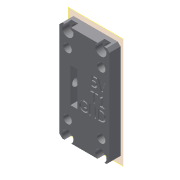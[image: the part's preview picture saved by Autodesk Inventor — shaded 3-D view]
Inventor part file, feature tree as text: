
AUTODESK INVENTOR PART (.ipt)
format: ipt  version: 2019 (Build 230136000, 136)  size: 431,104 bytes
history: native  units: mm
features: sketch x7, extrude x6, projected_geometry x5, other x3, plane x1, hole x1, reference x1
ambient origin geometry x8: Origin, YZ Plane, XZ Plane, XY Plane, X Axis, Y Axis, Z Axis, Center Point
bodies: Volumenkörper1 (feature_tree)
feature tree (24):
  plane  "Arbeitsebene1"
  extrude  "Extrusion1"  Depth=1.0mm TaperAngle=0.0deg
  hole  "Bohrung1"  [1 undecoded]
  extrude  "Extrusion3"  Depth=10.0mm
  extrude  "Extrusion4"  Depth=10.0mm
  extrude  "Extrusion5"  Depth=22.0mm
  extrude  "Extrusion6"  Depth=1.0mm
  extrude  "Extrusion7"  Depth=3.0mm
  sketch  "Skizze1"  dims[d0=4.0mm d1=0.0mm]
  reference  "Referenz1"
  sketch  "Skizze2"  dims[d2=2.0mm d3=6.0mm d4=4.0mm d5=2.5mm d6=90.0deg d7=12.0mm d8=20.594885mm d28=1.0mm d29=0.0mm]
  projected_geometry  "Projizierte Kontur1"
  sketch  "Skizze5"  dims[d31=12.3mm d32=2.5mm]
  sketch  "Skizze6"  dims[d33=10.0mm d34=0.0mm d35=2.8mm]
  projected_geometry  "Projizierte Kontur4"
  sketch  "Skizze7"  dims[d36=10.0mm d37=0.0mm d38=17.9mm]
  projected_geometry  "Projizierte Kontur5"
  sketch  "Skizze8"  dims[d39=12.0mm d40=22.0mm]
  projected_geometry  "Projizierte Kontur6"
  sketch  "Skizze9"  dims[d41=17.9mm d42=8.9mm d43=3.0mm d44=3.0mm d45=3.0mm d46=3.0mm d47=3.0mm d48=-0.698132mm d49=0.4mm d50=1.0mm d51=0.0mm]
  projected_geometry  "Projizierte Kontur7"
  other  "Assembly_Omniscope_v1.iam"
  other  "01_Camera_Module_left_v0:1"
  other  "<userpath>\Documents\Inventor\HITscope\Assembly_Omniscope_v1.iam"
note: 1 required parameter value undecoded (feature->parameter linkage not recoverable at this tier; creation-order binding heuristic only, values carry confidence <= 0.55)
